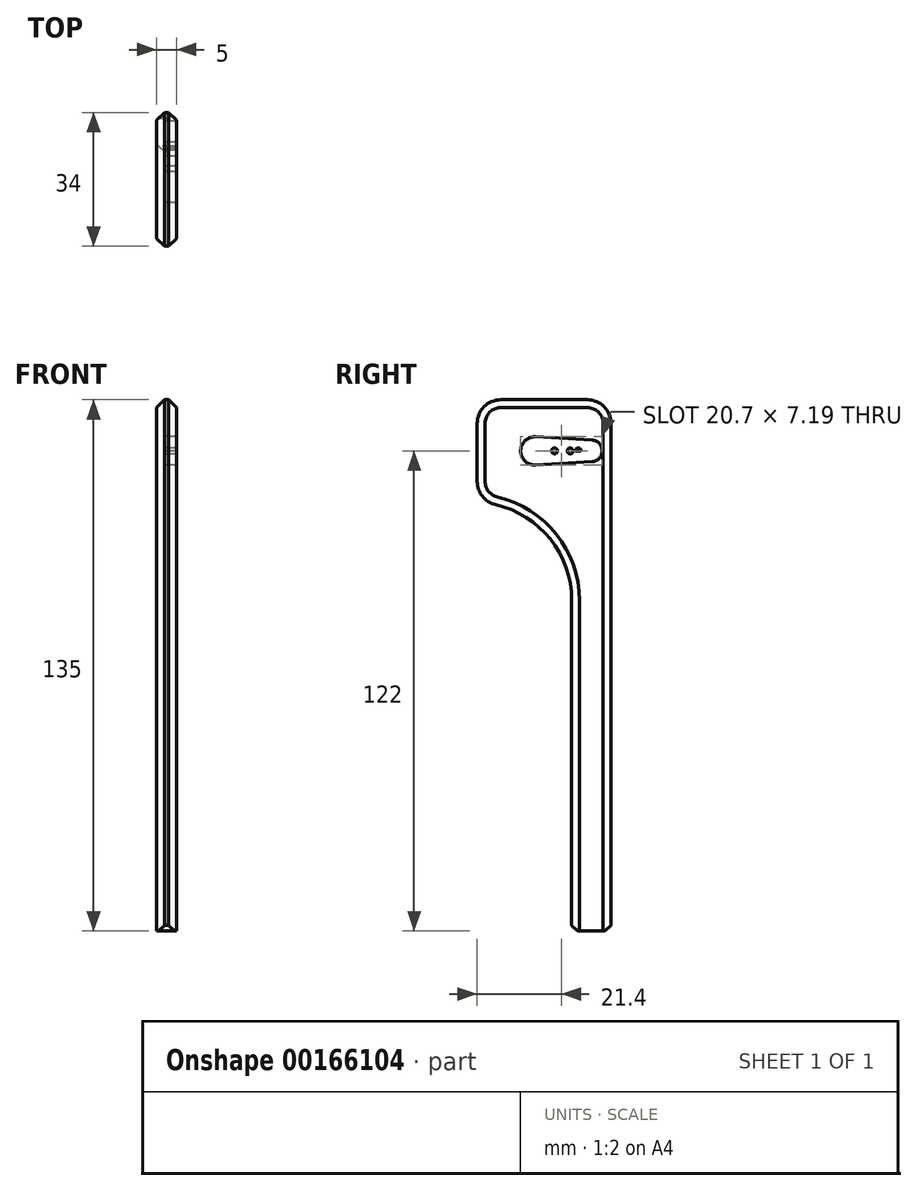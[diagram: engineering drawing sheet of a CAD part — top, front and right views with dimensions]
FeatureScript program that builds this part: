
annotation { "Feature Type Name" : "Feature", "Feature Type Description" : "" }
export const myFeature = defineFeature(function(context is Context, id is Id, definition is map)
    precondition{}
    {
        {
            var Q0;
            Q0=qCreatedBy(makeId("Right.planeOp"),FACE);
            var sketch = newSketch(context, id + "F0", { "sketchPlane" : qUnion([Q0])});
            skLineSegment(sketch, "E0.bottom", {"start": v(-12, 13) * mm, "end": v(12, 13) * mm});
            skLineSegment(sketch, "E0.top", {"start": v(-12, -13) * mm, "end": v(12, -13) * mm});
            skLineSegment(sketch, "E0.left", {"start": v(-12, 13) * mm, "end": v(-12, -13) * mm});
            skLineSegment(sketch, "E0.right", {"start": v(12, 13) * mm, "end": v(12, -13) * mm});
            skPoint(sketch, "E0.middle", {"position": v(0, 0) * mm});
            skLineSegment(sketch, "E1.bottom", {"start": v(12, 13) * mm, "end": v(22, 13) * mm});
            skLineSegment(sketch, "E1.top", {"start": v(12, -122) * mm, "end": v(22, -122) * mm});
            skLineSegment(sketch, "E1.left", {"start": v(12, 13) * mm, "end": v(12, -122) * mm});
            skLineSegment(sketch, "E1.right", {"start": v(22, 13) * mm, "end": v(22, -122) * mm});
            skSolve(sketch);
        }
        {
            var Q0;
            {var subQ0=sQuery(id+"F0.wireOp",EDGE,"E0.bottom");Q0=makeQuery(id+"F0.imprint","IMPRINT",FACE,{"disambiguationData":[TD([[makeQuery(id+"F0.imprint","IMPRINT",EDGE,{"derivedFrom":subQ0}),-1.0]])]});}
            var Q1;
            {var subQ3=sQuery(id+"F0.wireOp",EDGE,"E1.bottom");Q1=makeQuery(id+"F0.imprint","IMPRINT",FACE,{"disambiguationData":[TD([[makeQuery(id+"F0.imprint","IMPRINT",EDGE,{"derivedFrom":subQ3}),-1.0]])]});}
            extrude(context, id + "F1", {"entities" : qUnion([Q0, Q1]), "depth" : 5 * mm});
        }
        {
            var Q0;
            Q0=makeQuery(id+"F1.opExtrude","SWEPT_EDGE",EDGE,{"disambiguationData":[OSD([sQuery(id+"F0.wireOp",EDGE,"E0.top"),sQuery(id+"F0.wireOp",EDGE,"E1.left")])]});
            fillet(context, id + "F2", {"entities" : qUnion([Q0]), "radius" : 25 * mm, "tangentPropagation" : true, "allowEdgeOverflow" : false});
        }
        {
            var Q0;
            Q0=makeQuery(id+"F1.opExtrude","SWEPT_EDGE",EDGE,{"disambiguationData":[OSD([sQuery(id+"F0.wireOp",EDGE,"E1.top"),sQuery(id+"F0.wireOp",EDGE,"E1.left")])]});
            var Q1;
            Q1=makeQuery(id+"F1.opExtrude","SWEPT_EDGE",EDGE,{"disambiguationData":[OSD([sQuery(id+"F0.wireOp",EDGE,"E1.top"),sQuery(id+"F0.wireOp",EDGE,"E1.right")])]});
            chamfer(context, id + "F3", {"entities" : qUnion([Q0, Q1]), "width" : 1.5 * mm, "tangentPropagation" : true});
        }
        {
            var Q0;
            Q0=makeQuery(id+"F2.opFillet","BLEND_EDGE",EDGE,{"blendedFrom":[makeQuery(id+"F1.opExtrude","SWEPT_EDGE",EDGE,{"disambiguationData":[OSD([sQuery(id+"F0.wireOp",EDGE,"E0.top"),sQuery(id+"F0.wireOp",EDGE,"E1.left")])]}),makeQuery(id+"F1.opExtrude","SWEPT_FACE",FACE,{"disambiguationData":[OSD([sQuery(id+"F0.wireOp",EDGE,"E0.left")])]})],"blendedInto":[makeQuery(id+"F1.opExtrude","SWEPT_FACE",FACE,{"disambiguationData":[OSD([sQuery(id+"F0.wireOp",EDGE,"E0.left")])]})]});
            var Q1;
            Q1=makeQuery(id+"F1.opExtrude","SWEPT_EDGE",EDGE,{"disambiguationData":[OSD([sQuery(id+"F0.wireOp",EDGE,"E0.bottom"),sQuery(id+"F0.wireOp",EDGE,"E0.left")])]});
            var Q2;
            Q2=makeQuery(id+"F1.opExtrude","SWEPT_EDGE",EDGE,{"disambiguationData":[OSD([sQuery(id+"F0.wireOp",EDGE,"E1.bottom"),sQuery(id+"F0.wireOp",EDGE,"E1.right")])]});
            fillet(context, id + "F4", {"entities" : qUnion([Q0, Q1, Q2]), "radius" : 6 * mm, "tangentPropagation" : true, "allowEdgeOverflow" : false});
        }
        {
            var Q0;
            Q0=makeQuery(id+"F1.opExtrude","CAP_EDGE",EDGE,{"disambiguationData":[OSD([sQuery(id+"F0.wireOp",EDGE,"E1.right")])],"isStart":false});
            var Q1;
            Q1=makeQuery(id+"F1.opExtrude","CAP_EDGE",EDGE,{"disambiguationData":[OSD([sQuery(id+"F0.wireOp",EDGE,"E1.right")])],"isStart":true});
            chamfer(context, id + "F5", {"entities" : qUnion([Q0, Q1]), "width" : 2 * mm, "tangentPropagation" : true});
        }
        {
            var Q0;
            Q0=makeQuery(id+"F1.opExtrude","CAP_FACE",FACE,{"disambiguationData":[OSD([sQuery(id+"F0.wireOp",EDGE,"E0.bottom"),sQuery(id+"F0.wireOp",EDGE,"E0.top"),sQuery(id+"F0.wireOp",EDGE,"E0.left"),sQuery(id+"F0.wireOp",EDGE,"E1.bottom"),sQuery(id+"F0.wireOp",EDGE,"E1.top"),sQuery(id+"F0.wireOp",EDGE,"E1.left"),sQuery(id+"F0.wireOp",EDGE,"E1.right")])],"isStart":true});
            var sketch = newSketch(context, id + "F6", { "sketchPlane" : qUnion([Q0])});
            skCircle(sketch, "E2", {"center": v(-2.65, 0) * mm, "radius": 2.6 * mm});
            skCircle(sketch, "E3", {"center": v(-2.65, 0) * mm, "radius": 3.6 * mm});
            skCircle(sketch, "E4", {"center": v(-17, 0) * mm, "radius": 2.75 * mm});
            skLineSegment(sketch, "E5", {"start": v(-2.86, -3.6) * mm, "end": v(-17.16, -2.75) * mm});
            skLineSegment(sketch, "E6", {"start": v(-17.16, 2.75) * mm, "end": v(-2.86, 3.6) * mm});
            skLineSegment(sketch, "E7", {"start": v(-17, 0) * mm, "end": v(-2.65, 0) * mm});
            skCircle(sketch, "E8", {"center": v(-7.65, 0) * mm, "radius": 0.75 * mm});
            skCircle(sketch, "E9", {"center": v(-9.65, 0) * mm, "radius": 0.75 * mm});
            skCircle(sketch, "E10", {"center": v(-11.65, 0) * mm, "radius": 0.75 * mm});
            skCircle(sketch, "E11", {"center": v(-13.65, 0) * mm, "radius": 0.75 * mm});
            skCircle(sketch, "E12", {"center": v(-15.65, 0) * mm, "radius": 0.75 * mm});
            skCircle(sketch, "E13", {"center": v(-17.65, 0) * mm, "radius": 0.75 * mm});
            skSolve(sketch);
        }
        {
            var Q0;
            Q0=makeQuery(id+"F6.imprint","IMPRINT",FACE,{"disambiguationData":[TD([[makeQuery(id+"F6.imprint","IMPRINT",EDGE,{"derivedFrom":sQuery(id+"F6.wireOp",EDGE,"E13")}),1.0]])]});
            var Q1;
            {var subQ0=sQuery(id+"F6.wireOp",EDGE,"E12");var subQ1=sQuery(id+"F6.wireOp",EDGE,"E7");var subQ2=makeQuery(id+"F6.imprint","INTERSECT",VERTEX,{"disambiguationData":[OD(0.0)],"derivedFrom":[subQ1,subQ0]});Q1=makeQuery(id+"F6.imprint","IMPRINT",FACE,{"disambiguationData":[TD([[makeQuery(id+"F6.imprint","IMPRINT",EDGE,{"disambiguationData":[TD([[subQ2,1.0]])],"derivedFrom":subQ1}),1.0]])]});}
            var Q2;
            {var subQ0=sQuery(id+"F6.wireOp",EDGE,"E12");var subQ1=sQuery(id+"F6.wireOp",EDGE,"E7");var subQ2=makeQuery(id+"F6.imprint","INTERSECT",VERTEX,{"disambiguationData":[OD(0.0)],"derivedFrom":[subQ1,subQ0]});Q2=makeQuery(id+"F6.imprint","IMPRINT",FACE,{"disambiguationData":[TD([[makeQuery(id+"F6.imprint","IMPRINT",EDGE,{"disambiguationData":[TD([[subQ2,1.0]])],"derivedFrom":subQ1}),-1.0]])]});}
            var Q3;
            {var subQ0=sQuery(id+"F6.wireOp",EDGE,"E11");var subQ1=sQuery(id+"F6.wireOp",EDGE,"E4");var subQ2=makeQuery(id+"F6.imprint","INTERSECT",VERTEX,{"disambiguationData":[OD(0.0)],"derivedFrom":[subQ1,subQ0]});Q3=makeQuery(id+"F6.imprint","IMPRINT",FACE,{"disambiguationData":[TD([[makeQuery(id+"F6.imprint","IMPRINT",EDGE,{"disambiguationData":[TD([[subQ2,1.0]])],"derivedFrom":subQ1}),-1.0]])]});}
            var Q4;
            {var subQ0=sQuery(id+"F6.wireOp",EDGE,"E7");var subQ1=sQuery(id+"F6.wireOp",EDGE,"E4");var subQ2=makeQuery(id+"F6.imprint","INTERSECT",VERTEX,{"derivedFrom":[subQ1,subQ0]});Q4=makeQuery(id+"F6.imprint","IMPRINT",FACE,{"disambiguationData":[TD([[makeQuery(id+"F6.imprint","IMPRINT",EDGE,{"disambiguationData":[TD([[subQ2,1.0]])],"derivedFrom":subQ1}),-1.0]])]});}
            var Q5;
            {var subQ0=sQuery(id+"F6.wireOp",EDGE,"E7");var subQ1=sQuery(id+"F6.wireOp",EDGE,"E4");var subQ2=makeQuery(id+"F6.imprint","INTERSECT",VERTEX,{"derivedFrom":[subQ1,subQ0]});Q5=makeQuery(id+"F6.imprint","IMPRINT",FACE,{"disambiguationData":[TD([[makeQuery(id+"F6.imprint","IMPRINT",EDGE,{"disambiguationData":[TD([[subQ2,1.0]])],"derivedFrom":subQ1}),1.0]])]});}
            var Q6;
            {var subQ0=sQuery(id+"F6.wireOp",EDGE,"E11");var subQ1=sQuery(id+"F6.wireOp",EDGE,"E4");var subQ2=makeQuery(id+"F6.imprint","INTERSECT",VERTEX,{"disambiguationData":[OD(0.0)],"derivedFrom":[subQ1,subQ0]});Q6=makeQuery(id+"F6.imprint","IMPRINT",FACE,{"disambiguationData":[TD([[makeQuery(id+"F6.imprint","IMPRINT",EDGE,{"disambiguationData":[TD([[subQ2,1.0]])],"derivedFrom":subQ1}),1.0]])]});}
            var Q7;
            {var subQ0=sQuery(id+"F6.wireOp",EDGE,"E10");var subQ1=sQuery(id+"F6.wireOp",EDGE,"E7");var subQ2=makeQuery(id+"F6.imprint","INTERSECT",VERTEX,{"disambiguationData":[OD(0.0)],"derivedFrom":[subQ1,subQ0]});Q7=makeQuery(id+"F6.imprint","IMPRINT",FACE,{"disambiguationData":[TD([[makeQuery(id+"F6.imprint","IMPRINT",EDGE,{"disambiguationData":[TD([[subQ2,-1.0]])],"derivedFrom":subQ1}),1.0]])]});}
            var Q8;
            {var subQ0=sQuery(id+"F6.wireOp",EDGE,"E10");var subQ1=sQuery(id+"F6.wireOp",EDGE,"E7");var subQ2=makeQuery(id+"F6.imprint","INTERSECT",VERTEX,{"disambiguationData":[OD(0.0)],"derivedFrom":[subQ1,subQ0]});Q8=makeQuery(id+"F6.imprint","IMPRINT",FACE,{"disambiguationData":[TD([[makeQuery(id+"F6.imprint","IMPRINT",EDGE,{"disambiguationData":[TD([[subQ2,-1.0]])],"derivedFrom":subQ1}),-1.0]])]});}
            var Q9;
            {var subQ0=sQuery(id+"F6.wireOp",EDGE,"E9");var subQ1=sQuery(id+"F6.wireOp",EDGE,"E7");var subQ2=makeQuery(id+"F6.imprint","INTERSECT",VERTEX,{"disambiguationData":[OD(0.0)],"derivedFrom":[subQ1,subQ0]});Q9=makeQuery(id+"F6.imprint","IMPRINT",FACE,{"disambiguationData":[TD([[makeQuery(id+"F6.imprint","IMPRINT",EDGE,{"disambiguationData":[TD([[subQ2,-1.0]])],"derivedFrom":subQ1}),-1.0]])]});}
            var Q10;
            {var subQ0=sQuery(id+"F6.wireOp",EDGE,"E9");var subQ1=sQuery(id+"F6.wireOp",EDGE,"E7");var subQ2=makeQuery(id+"F6.imprint","INTERSECT",VERTEX,{"disambiguationData":[OD(0.0)],"derivedFrom":[subQ1,subQ0]});Q10=makeQuery(id+"F6.imprint","IMPRINT",FACE,{"disambiguationData":[TD([[makeQuery(id+"F6.imprint","IMPRINT",EDGE,{"disambiguationData":[TD([[subQ2,-1.0]])],"derivedFrom":subQ1}),1.0]])]});}
            var Q11;
            {var subQ0=sQuery(id+"F6.wireOp",EDGE,"E8");var subQ1=sQuery(id+"F6.wireOp",EDGE,"E7");var subQ2=makeQuery(id+"F6.imprint","INTERSECT",VERTEX,{"disambiguationData":[OD(0.0)],"derivedFrom":[subQ1,subQ0]});Q11=makeQuery(id+"F6.imprint","IMPRINT",FACE,{"disambiguationData":[TD([[makeQuery(id+"F6.imprint","IMPRINT",EDGE,{"disambiguationData":[TD([[subQ2,-1.0]])],"derivedFrom":subQ1}),1.0]])]});}
            var Q12;
            {var subQ0=sQuery(id+"F6.wireOp",EDGE,"E8");var subQ1=sQuery(id+"F6.wireOp",EDGE,"E7");var subQ2=makeQuery(id+"F6.imprint","INTERSECT",VERTEX,{"disambiguationData":[OD(0.0)],"derivedFrom":[subQ1,subQ0]});Q12=makeQuery(id+"F6.imprint","IMPRINT",FACE,{"disambiguationData":[TD([[makeQuery(id+"F6.imprint","IMPRINT",EDGE,{"disambiguationData":[TD([[subQ2,-1.0]])],"derivedFrom":subQ1}),-1.0]])]});}
            var Q13;
            Q13=makeQuery(id+"F6.imprint","IMPRINT",FACE,{"disambiguationData":[TD([[makeQuery(id+"F6.imprint","IMPRINT",EDGE,{"derivedFrom":sQuery(id+"F6.wireOp",EDGE,"E2")}),1.0]])]});
            var Q14;
            Q14=makeQuery(id+"F6.imprint","IMPRINT",FACE,{"disambiguationData":[TD([[makeQuery(id+"F6.imprint","IMPRINT",EDGE,{"derivedFrom":sQuery(id+"F6.wireOp",EDGE,"E2")}),-1.0]])]});
            extrude(context, id + "F7", {"entities" : qUnion([Q0, Q1, Q2, Q3, Q4, Q5, Q6, Q7, Q8, Q9, Q10, Q11, Q12, Q13, Q14]), "operationType" : NewBodyOperationType.REMOVE, "oppositeDirection" : true, "depth" : 5 * mm});
        }
        {
            var Q0;
            {var subQ11=sQuery(id+"F6.wireOp",EDGE,"E5");Q0=makeQuery(id+"F6.imprint","IMPRINT",FACE,{"disambiguationData":[TD([[makeQuery(id+"F6.imprint","IMPRINT",EDGE,{"derivedFrom":subQ11}),-1.0]])]});}
            var Q1;
            Q1=makeQuery(id+"F6.imprint","IMPRINT",FACE,{"disambiguationData":[TD([[makeQuery(id+"F6.imprint","IMPRINT",EDGE,{"derivedFrom":sQuery(id+"F6.wireOp",EDGE,"E13")}),-1.0]])]});
            var Q2;
            {var subQ11=sQuery(id+"F6.wireOp",EDGE,"E6");Q2=makeQuery(id+"F6.imprint","IMPRINT",FACE,{"disambiguationData":[TD([[makeQuery(id+"F6.imprint","IMPRINT",EDGE,{"derivedFrom":subQ11}),-1.0]])]});}
            extrude(context, id + "F8", {"entities" : qUnion([Q0, Q1, Q2]), "operationType" : NewBodyOperationType.REMOVE, "oppositeDirection" : true, "depth" : 2.5 * mm});
        }
    });
